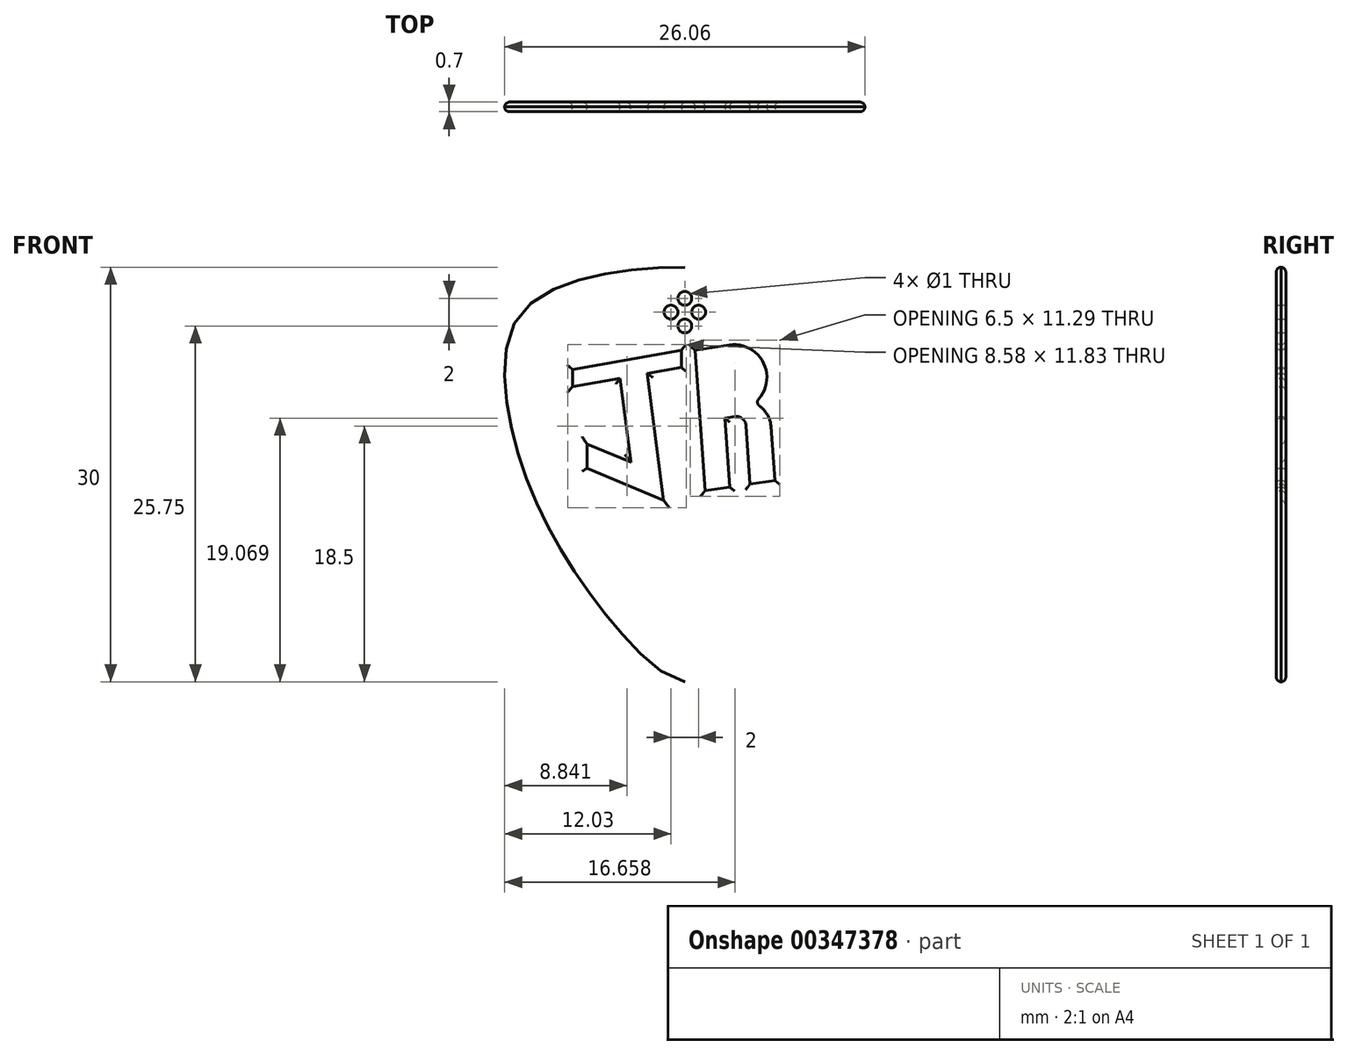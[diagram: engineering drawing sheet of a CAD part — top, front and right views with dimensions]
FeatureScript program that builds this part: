
annotation { "Feature Type Name" : "Feature", "Feature Type Description" : "" }
export const myFeature = defineFeature(function(context is Context, id is Id, definition is map)
    precondition{}
    {
        {
            var Q0;
            Q0=qCreatedBy(makeId("Front.planeOp"),FACE);
            var sketch = newSketch(context, id + "F0", { "sketchPlane" : qUnion([Q0])});
            skLineSegment(sketch, "E0", {"start": v(0, 0) * mm, "end": v(0, 6.75) * mm, "construction": true});
            skLineSegment(sketch, "E1", {"start": v(0, 0) * mm, "end": v(0, -23.25) * mm, "construction": true});
            skLineSegment(sketch, "E2", {"start": v(0, 0) * mm, "end": v(13, 0) * mm, "construction": true});
            skFitSpline(sketch, "E3", {"points": [v(0, -23.25) * mm, v(9.5, -12.75) * mm, v(13, 0) * mm, v(11, 4.25) * mm, v(0, 6.75) * mm], "startDerivative": vector(20.6, 0) * mm, "endDerivative": vector(-57.72, 0) * mm});
            skFitSpline(sketch, "E4.MirrorCS", {"points": [v(0, -23.25) * mm, v(-9.5, -12.75) * mm, v(-13, 0) * mm, v(-11, 4.25) * mm, v(0, 6.75) * mm], "startDerivative": vector(-20.6, 0) * mm, "endDerivative": vector(57.72, 0) * mm});
            skLineSegment(sketch, "E5", {"start": v(0.75, 0.75) * mm, "end": v(1.46, -9.43) * mm});
            skLineSegment(sketch, "E6", {"start": v(1.46, -9.43) * mm, "end": v(3.24, -9.16) * mm});
            skLineSegment(sketch, "E7", {"start": v(3.24, -9.16) * mm, "end": v(2.9, -4.17) * mm});
            skLineSegment(sketch, "E8", {"start": v(2.9, -4.17) * mm, "end": v(3.63, -4.06) * mm});
            skLineSegment(sketch, "E9", {"start": v(4.73, -8.94) * mm, "end": v(4.43, -4.7) * mm});
            skLineSegment(sketch, "E10", {"start": v(3.24, -9.16) * mm, "end": v(4.73, -8.94) * mm, "construction": true});
            skLineSegment(sketch, "E11", {"start": v(4.73, -8.94) * mm, "end": v(6.5, -8.67) * mm});
            skArc(sketch, "E12", {"start": v(4.43, -4.7) * mm, "mid": v(4.17, -4.2) * mm, "end": v(3.63, -4.06) * mm});
            skLineSegment(sketch, "E13", {"start": v(6.5, -8.67) * mm, "end": v(6.23, -4.78) * mm});
            skLineSegment(sketch, "E14", {"start": v(0.75, 0.75) * mm, "end": v(3.22, 1.12) * mm});
            skArc(sketch, "E15", {"start": v(5.03, -3.08) * mm, "mid": v(5.74, -0.29) * mm, "end": v(3.22, 1.12) * mm});
            skArc(sketch, "E16", {"start": v(6.23, -4.78) * mm, "mid": v(5.87, -3.76) * mm, "end": v(5.03, -3.08) * mm});
            skLineSegment(sketch, "E17", {"start": v(-2.7, -0.93) * mm, "end": v(-1.54, -10.1) * mm});
            skLineSegment(sketch, "E18", {"start": v(-1.54, -10.1) * mm, "end": v(-7.08, -7.79) * mm});
            skLineSegment(sketch, "E19", {"start": v(-7.08, -7.79) * mm, "end": v(-7.08, -6.04) * mm});
            skLineSegment(sketch, "E20", {"start": v(-7.08, -6.04) * mm, "end": v(-3.9, -7.37) * mm});
            skLineSegment(sketch, "E21", {"start": v(-3.9, -7.37) * mm, "end": v(-4.68, -1.28) * mm});
            skLineSegment(sketch, "E22", {"start": v(-4.68, -1.28) * mm, "end": v(-8.13, -1.89) * mm});
            skLineSegment(sketch, "E23", {"start": v(-8.13, -1.89) * mm, "end": v(-8.13, -0.64) * mm});
            skLineSegment(sketch, "E24", {"start": v(-8.13, -0.64) * mm, "end": v(-0.25, 0.75) * mm});
            skLineSegment(sketch, "E25", {"start": v(-0.25, 0.75) * mm, "end": v(-0.25, -0.5) * mm});
            skLineSegment(sketch, "E26", {"start": v(-0.25, -0.5) * mm, "end": v(-2.7, -0.93) * mm});
            skLineSegment(sketch, "E27", {"start": v(-4.68, -1.28) * mm, "end": v(-2.7, -0.93) * mm, "construction": true});
            skCircle(sketch, "E28", {"center": v(0, 4.5) * mm, "radius": 0.5 * mm});
            skCircle(sketch, "E29", {"center": v(0, 2.5) * mm, "radius": 0.5 * mm});
            skLineSegment(sketch, "E30", {"start": v(0, 3.5) * mm, "end": v(1, 3.5) * mm});
            skCircle(sketch, "E31", {"center": v(1, 3.5) * mm, "radius": 0.5 * mm});
            skLineSegment(sketch, "E32", {"start": v(0, 4.5) * mm, "end": v(0, 3.5) * mm});
            skLineSegment(sketch, "E33", {"start": v(0, 3.5) * mm, "end": v(0, 2.5) * mm});
            skLineSegment(sketch, "E34.MirrorCS", {"start": v(0, 3.5) * mm, "end": v(-1, 3.5) * mm});
            skCircle(sketch, "E35.MirrorC", {"center": v(-1, 3.5) * mm, "radius": 0.5 * mm});
            skSolve(sketch);
        }
        {
            var Q0;
            Q0=qSketchRegion(id+"F0",true);
            extrude(context, id + "F1", {"entities" : qUnion([Q0]), "depth" : 0.7 * mm});
        }
        {
            var Q0;
            Q0=makeQuery(id+"F1.opExtrude","CAP_EDGE",EDGE,{"disambiguationData":[OSD([sQuery(id+"F0.wireOp",EDGE,"E4.MirrorCS")])],"isStart":false});
            var Q1;
            Q1=makeQuery(id+"F1.opExtrude","CAP_EDGE",EDGE,{"disambiguationData":[OSD([sQuery(id+"F0.wireOp",EDGE,"E3")])],"isStart":false});
            var Q2;
            Q2=makeQuery(id+"F1.opExtrude","CAP_EDGE",EDGE,{"disambiguationData":[OSD([sQuery(id+"F0.wireOp",EDGE,"E4.MirrorCS")])],"isStart":true});
            var Q3;
            Q3=makeQuery(id+"F1.opExtrude","CAP_EDGE",EDGE,{"disambiguationData":[OSD([sQuery(id+"F0.wireOp",EDGE,"E3")])],"isStart":true});
            fillet(context, id + "F2", {"entities" : qUnion([Q0, Q1, Q2, Q3]), "radius" : 0.7 / 2 * mm, "tangentPropagation" : true, "allowEdgeOverflow" : false});
        }
        {
            var Q0;
            Q0=makeQuery(id+"F1.opExtrude","CAP_EDGE",EDGE,{"disambiguationData":[OSD([sQuery(id+"F0.wireOp",EDGE,"E20")])],"isStart":false});
            var Q1;
            Q1=makeQuery(id+"F1.opExtrude","CAP_EDGE",EDGE,{"disambiguationData":[OSD([sQuery(id+"F0.wireOp",EDGE,"E21")])],"isStart":false});
            var Q2;
            Q2=makeQuery(id+"F1.opExtrude","CAP_EDGE",EDGE,{"disambiguationData":[OSD([sQuery(id+"F0.wireOp",EDGE,"E19")])],"isStart":false});
            var Q3;
            Q3=makeQuery(id+"F1.opExtrude","CAP_EDGE",EDGE,{"disambiguationData":[OSD([sQuery(id+"F0.wireOp",EDGE,"E18")])],"isStart":false});
            var Q4;
            Q4=makeQuery(id+"F1.opExtrude","CAP_EDGE",EDGE,{"disambiguationData":[OSD([sQuery(id+"F0.wireOp",EDGE,"E17")])],"isStart":false});
            var Q5;
            Q5=makeQuery(id+"F1.opExtrude","CAP_EDGE",EDGE,{"disambiguationData":[OSD([sQuery(id+"F0.wireOp",EDGE,"E26")])],"isStart":false});
            var Q6;
            Q6=makeQuery(id+"F1.opExtrude","CAP_EDGE",EDGE,{"disambiguationData":[OSD([sQuery(id+"F0.wireOp",EDGE,"E25")])],"isStart":false});
            var Q7;
            Q7=makeQuery(id+"F1.opExtrude","CAP_EDGE",EDGE,{"disambiguationData":[OSD([sQuery(id+"F0.wireOp",EDGE,"E24")])],"isStart":false});
            var Q8;
            Q8=makeQuery(id+"F1.opExtrude","CAP_EDGE",EDGE,{"disambiguationData":[OSD([sQuery(id+"F0.wireOp",EDGE,"E23")])],"isStart":false});
            var Q9;
            Q9=makeQuery(id+"F1.opExtrude","CAP_EDGE",EDGE,{"disambiguationData":[OSD([sQuery(id+"F0.wireOp",EDGE,"E22")])],"isStart":false});
            var Q10;
            Q10=makeQuery(id+"F1.opExtrude","CAP_EDGE",EDGE,{"disambiguationData":[OSD([sQuery(id+"F0.wireOp",EDGE,"E14")])],"isStart":false});
            var Q11;
            Q11=makeQuery(id+"F1.opExtrude","CAP_EDGE",EDGE,{"disambiguationData":[OSD([sQuery(id+"F0.wireOp",EDGE,"E15")])],"isStart":false});
            var Q12;
            Q12=makeQuery(id+"F1.opExtrude","CAP_EDGE",EDGE,{"disambiguationData":[OSD([sQuery(id+"F0.wireOp",EDGE,"E5")])],"isStart":false});
            var Q13;
            Q13=makeQuery(id+"F1.opExtrude","CAP_EDGE",EDGE,{"disambiguationData":[OSD([sQuery(id+"F0.wireOp",EDGE,"E6")])],"isStart":false});
            var Q14;
            Q14=makeQuery(id+"F1.opExtrude","CAP_EDGE",EDGE,{"disambiguationData":[OSD([sQuery(id+"F0.wireOp",EDGE,"E7")])],"isStart":false});
            var Q15;
            Q15=makeQuery(id+"F1.opExtrude","CAP_EDGE",EDGE,{"disambiguationData":[OSD([sQuery(id+"F0.wireOp",EDGE,"E8")])],"isStart":false});
            var Q16;
            Q16=makeQuery(id+"F1.opExtrude","CAP_EDGE",EDGE,{"disambiguationData":[OSD([sQuery(id+"F0.wireOp",EDGE,"E11")])],"isStart":false});
            var Q17;
            Q17=makeQuery(id+"F1.opExtrude","CAP_EDGE",EDGE,{"disambiguationData":[OSD([sQuery(id+"F0.wireOp",EDGE,"E13")])],"isStart":false});
            var Q18;
            Q18=makeQuery(id+"F1.opExtrude","CAP_EDGE",EDGE,{"disambiguationData":[OSD([sQuery(id+"F0.wireOp",EDGE,"E16")])],"isStart":false});
            var Q19;
            Q19=makeQuery(id+"F1.opExtrude","CAP_EDGE",EDGE,{"disambiguationData":[OSD([sQuery(id+"F0.wireOp",EDGE,"E11")])],"isStart":true});
            var Q20;
            Q20=makeQuery(id+"F1.opExtrude","CAP_EDGE",EDGE,{"disambiguationData":[OSD([sQuery(id+"F0.wireOp",EDGE,"E9")])],"isStart":true});
            var Q21;
            Q21=makeQuery(id+"F1.opExtrude","CAP_EDGE",EDGE,{"disambiguationData":[OSD([sQuery(id+"F0.wireOp",EDGE,"E13")])],"isStart":true});
            var Q22;
            Q22=makeQuery(id+"F1.opExtrude","CAP_EDGE",EDGE,{"disambiguationData":[OSD([sQuery(id+"F0.wireOp",EDGE,"E15")])],"isStart":true});
            var Q23;
            Q23=makeQuery(id+"F1.opExtrude","CAP_EDGE",EDGE,{"disambiguationData":[OSD([sQuery(id+"F0.wireOp",EDGE,"E14")])],"isStart":true});
            var Q24;
            Q24=makeQuery(id+"F1.opExtrude","CAP_EDGE",EDGE,{"disambiguationData":[OSD([sQuery(id+"F0.wireOp",EDGE,"E5")])],"isStart":true});
            var Q25;
            Q25=makeQuery(id+"F1.opExtrude","CAP_EDGE",EDGE,{"disambiguationData":[OSD([sQuery(id+"F0.wireOp",EDGE,"E8")])],"isStart":true});
            var Q26;
            Q26=makeQuery(id+"F1.opExtrude","CAP_EDGE",EDGE,{"disambiguationData":[OSD([sQuery(id+"F0.wireOp",EDGE,"E7")])],"isStart":true});
            var Q27;
            Q27=makeQuery(id+"F1.opExtrude","CAP_EDGE",EDGE,{"disambiguationData":[OSD([sQuery(id+"F0.wireOp",EDGE,"E6")])],"isStart":true});
            var Q28;
            Q28=makeQuery(id+"F1.opExtrude","CAP_EDGE",EDGE,{"disambiguationData":[OSD([sQuery(id+"F0.wireOp",EDGE,"E17")])],"isStart":true});
            var Q29;
            Q29=makeQuery(id+"F1.opExtrude","CAP_EDGE",EDGE,{"disambiguationData":[OSD([sQuery(id+"F0.wireOp",EDGE,"E18")])],"isStart":true});
            var Q30;
            Q30=makeQuery(id+"F1.opExtrude","CAP_EDGE",EDGE,{"disambiguationData":[OSD([sQuery(id+"F0.wireOp",EDGE,"E19")])],"isStart":true});
            var Q31;
            Q31=makeQuery(id+"F1.opExtrude","CAP_EDGE",EDGE,{"disambiguationData":[OSD([sQuery(id+"F0.wireOp",EDGE,"E20")])],"isStart":true});
            var Q32;
            Q32=makeQuery(id+"F1.opExtrude","CAP_EDGE",EDGE,{"disambiguationData":[OSD([sQuery(id+"F0.wireOp",EDGE,"E21")])],"isStart":true});
            var Q33;
            Q33=makeQuery(id+"F1.opExtrude","CAP_EDGE",EDGE,{"disambiguationData":[OSD([sQuery(id+"F0.wireOp",EDGE,"E22")])],"isStart":true});
            var Q34;
            Q34=makeQuery(id+"F1.opExtrude","CAP_EDGE",EDGE,{"disambiguationData":[OSD([sQuery(id+"F0.wireOp",EDGE,"E23")])],"isStart":true});
            var Q35;
            Q35=makeQuery(id+"F1.opExtrude","CAP_EDGE",EDGE,{"disambiguationData":[OSD([sQuery(id+"F0.wireOp",EDGE,"E24")])],"isStart":true});
            var Q36;
            Q36=makeQuery(id+"F1.opExtrude","CAP_EDGE",EDGE,{"disambiguationData":[OSD([sQuery(id+"F0.wireOp",EDGE,"E26")])],"isStart":true});
            var Q37;
            Q37=makeQuery(id+"F1.opExtrude","CAP_EDGE",EDGE,{"disambiguationData":[OSD([sQuery(id+"F0.wireOp",EDGE,"E25")])],"isStart":true});
            var Q38;
            Q38=makeQuery(id+"F1.opExtrude","SWEPT_EDGE",EDGE,{"disambiguationData":[OSD([sQuery(id+"F0.wireOp",EDGE,"E15"),sQuery(id+"F0.wireOp",EDGE,"E16")])]});
            var Q39;
            Q39=makeQuery(id+"F1.opExtrude","CAP_EDGE",EDGE,{"disambiguationData":[OSD([sQuery(id+"F0.wireOp",EDGE,"f2LN9vOS-7VoW-CH8w-TCzc-xVYya9SNDUs0")])],"isStart":false});
            var Q40;
            Q40=makeQuery(id+"F1.opExtrude","SWEPT_FACE",FACE,{"disambiguationData":[OSD([sQuery(id+"F0.wireOp",EDGE,"f2LN9vOS-7VoW-CH8w-TCzc-xVYya9SNDUs0")])]});
            fillet(context, id + "F3", {"entities" : qUnion([Q0, Q1, Q2, Q3, Q4, Q5, Q6, Q7, Q8, Q9, Q10, Q11, Q12, Q13, Q14, Q15, Q16, Q17, Q18, Q19, Q20, Q21, Q22, Q23, Q24, Q25, Q26, Q27, Q28, Q29, Q30, Q31, Q32, Q33, Q34, Q35, Q36, Q37, Q38, Q39, Q40]), "radius" : (0.7 / 2) * mm, "tangentPropagation" : true, "allowEdgeOverflow" : false});
        }
    });
